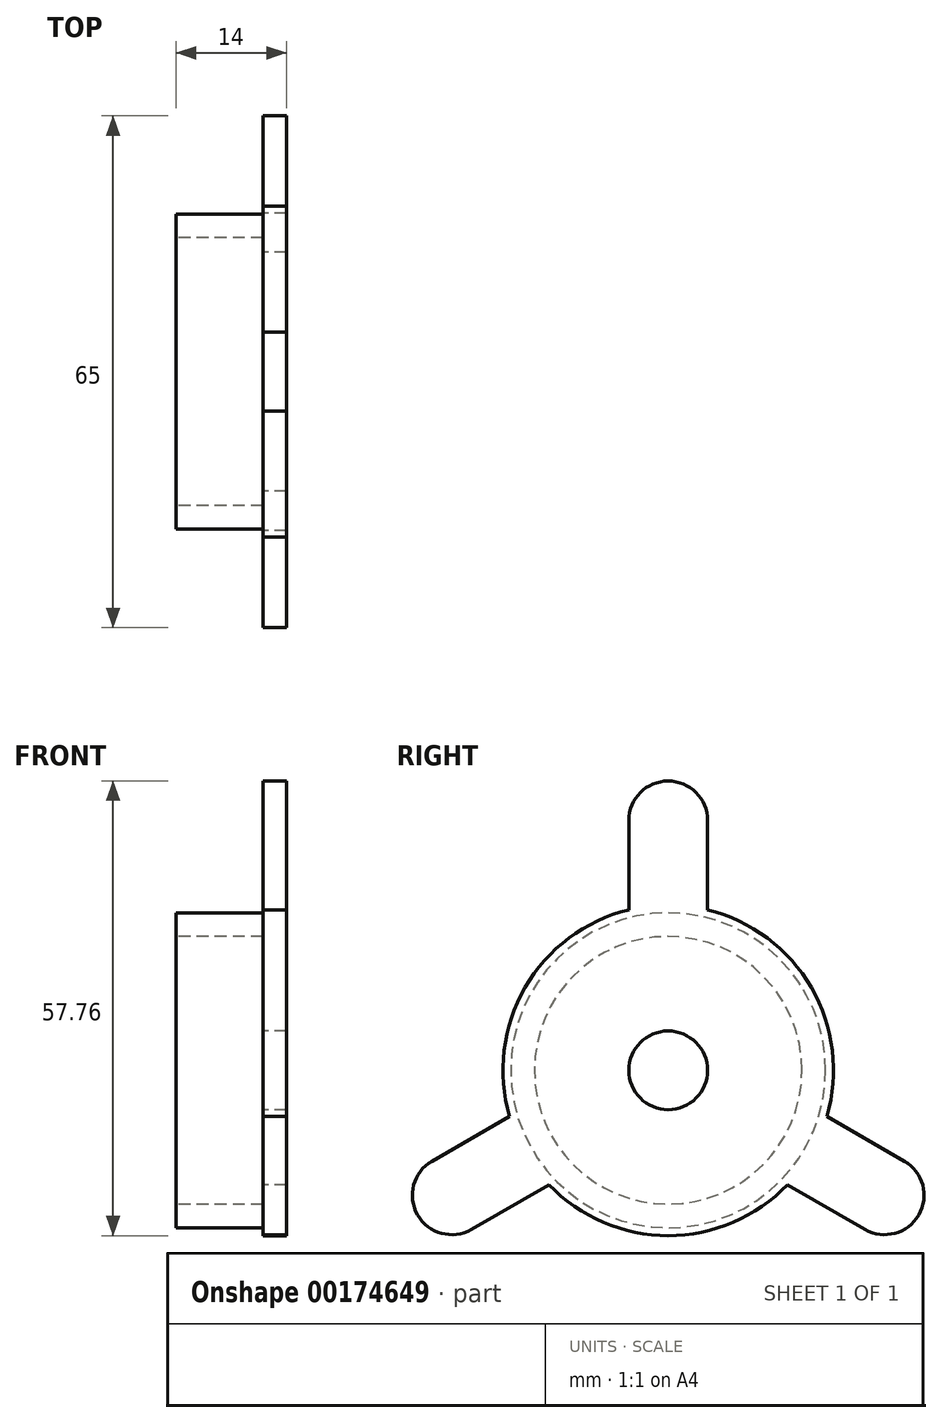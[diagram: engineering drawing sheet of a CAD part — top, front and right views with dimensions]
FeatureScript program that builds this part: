
annotation { "Feature Type Name" : "Feature", "Feature Type Description" : "" }
export const myFeature = defineFeature(function(context is Context, id is Id, definition is map)
    precondition{}
    {
        {
            var Q0;
            Q0=qCreatedBy(makeId("Front.planeOp"),FACE);
            var sketch = newSketch(context, id + "F0", { "sketchPlane" : qUnion([Q0])});
            skLineSegment(sketch, "E0", {"start": v(-46.36, 26.4) * mm, "end": v(-35.36, 26.4) * mm});
            skLineSegment(sketch, "E1", {"start": v(-35.36, 26.4) * mm, "end": v(-35.36, 27.4) * mm});
            skLineSegment(sketch, "E2", {"start": v(-35.36, 27.4) * mm, "end": v(-32.36, 27.4) * mm});
            skLineSegment(sketch, "E3", {"start": v(-32.36, 27.4) * mm, "end": v(-32.36, 11.4) * mm});
            skLineSegment(sketch, "E4", {"start": v(-32.36, 11.4) * mm, "end": v(-35.36, 11.4) * mm});
            skLineSegment(sketch, "E5", {"start": v(-35.36, 11.4) * mm, "end": v(-35.36, 23.4) * mm});
            skLineSegment(sketch, "E6", {"start": v(-35.36, 23.4) * mm, "end": v(-46.36, 23.4) * mm});
            skLineSegment(sketch, "E7", {"start": v(-46.36, 26.4) * mm, "end": v(-46.36, 23.4) * mm});
            skLineSegment(sketch, "E8", {"start": v(-35.36, 11.4) * mm, "end": v(-36.36, 11.4) * mm});
            skLineSegment(sketch, "E9", {"start": v(-36.36, 11.4) * mm, "end": v(-36.36, 12.4) * mm});
            skLineSegment(sketch, "E10", {"start": v(-36.36, 12.4) * mm, "end": v(-35.36, 12.4) * mm});
            skLineSegment(sketch, "E11", {"start": v(-32.36, 6.4) * mm, "end": v(-58.85, 6.4) * mm});
            skLineSegment(sketch, "E12", {"start": v(-58.85, 6.4) * mm, "end": v(-2.08, 6.4) * mm});
            skSolve(sketch);
        }
        {
            var Q0;
            Q0=makeQuery(id+"F0.imprint","IMPRINT",FACE,{"disambiguationData":[TD([[makeQuery(id+"F0.imprint","IMPRINT",EDGE,{"derivedFrom":sQuery(id+"F0.wireOp",EDGE,"E0")}),-1.0]])]});
            var Q1;
            Q1=sQuery(id+"F0.wireOp",EDGE,"E12");
            revolve(context, id + "F1", {"entities" : qUnion([Q0]), "axis" : qUnion([Q1]), "revolveType" : RevolveType.ONE_DIRECTION, "angle" : 360 * degree});
        }
        {
            var Q0;
            Q0=makeQuery(id+"F1.opRevolve","SWEPT_FACE",FACE,{"disambiguationData":[OSD([sQuery(id+"F0.wireOp",EDGE,"E1")])]});
            var sketch = newSketch(context, id + "F2", { "sketchPlane" : qUnion([Q0])});
            skArc(sketch, "E13", {"start": v(5, 38.16) * mm, "mid": v(0, 43.16) * mm, "end": v(-5, 38.16) * mm});
            skLineSegment(sketch, "E14", {"start": v(5, 38.16) * mm, "end": v(5, 26.8) * mm});
            skLineSegment(sketch, "E15", {"start": v(-5, 38.16) * mm, "end": v(-5, 26.8) * mm});
            skLineSegment(sketch, "E16", {"start": v(-5, 26.8) * mm, "end": v(-5.25, 28.08) * mm});
            skArc(sketch, "E17.1.0", {"start": v(-30, -5.14) * mm, "mid": v(-31.83, -11.97) * mm, "end": v(-25, -13.8) * mm});
            skLineSegment(sketch, "E17.1.1", {"start": v(-25, -13.8) * mm, "end": v(-15.16, -8.12) * mm});
            skLineSegment(sketch, "E17.1.2", {"start": v(-30, -5.14) * mm, "end": v(-20.16, 0.54) * mm});
            skLineSegment(sketch, "E17.1.3", {"start": v(-15.16, -8.12) * mm, "end": v(-16.15, -8.97) * mm});
            skArc(sketch, "E17.2.0", {"start": v(25, -13.8) * mm, "mid": v(31.83, -11.97) * mm, "end": v(30, -5.14) * mm});
            skLineSegment(sketch, "E17.2.1", {"start": v(30, -5.14) * mm, "end": v(20.16, 0.54) * mm});
            skLineSegment(sketch, "E17.2.2", {"start": v(25, -13.8) * mm, "end": v(15.16, -8.12) * mm});
            skLineSegment(sketch, "E17.2.3", {"start": v(20.16, 0.54) * mm, "end": v(21.4, 0.11) * mm});
            skPoint(sketch, "E17.center", {"position": v(0, 6.4) * mm});
            skSolve(sketch);
        }
        {
            var Q0;
            Q0=makeQuery(id+"F2.imprint","IMPRINT",FACE,{"disambiguationData":[TD([[makeQuery(id+"F2.imprint","IMPRINT",EDGE,{"derivedFrom":sQuery(id+"F2.wireOp",EDGE,"E13")}),1.0]])]});
            var Q1;
            Q1=makeQuery(id+"F2.imprint","IMPRINT",FACE,{"disambiguationData":[TD([[makeQuery(id+"F2.imprint","IMPRINT",EDGE,{"derivedFrom":sQuery(id+"F2.wireOp",EDGE,"E17.1.0")}),1.0]])]});
            var Q2;
            Q2=makeQuery(id+"F2.imprint","IMPRINT",FACE,{"disambiguationData":[TD([[makeQuery(id+"F2.imprint","IMPRINT",EDGE,{"derivedFrom":sQuery(id+"F2.wireOp",EDGE,"E17.2.0")}),1.0]])]});
            extrude(context, id + "F3", {"entities" : qUnion([Q0, Q1, Q2]), "operationType" : NewBodyOperationType.ADD, "oppositeDirection" : true, "depth" : 3 * mm});
        }
    });
